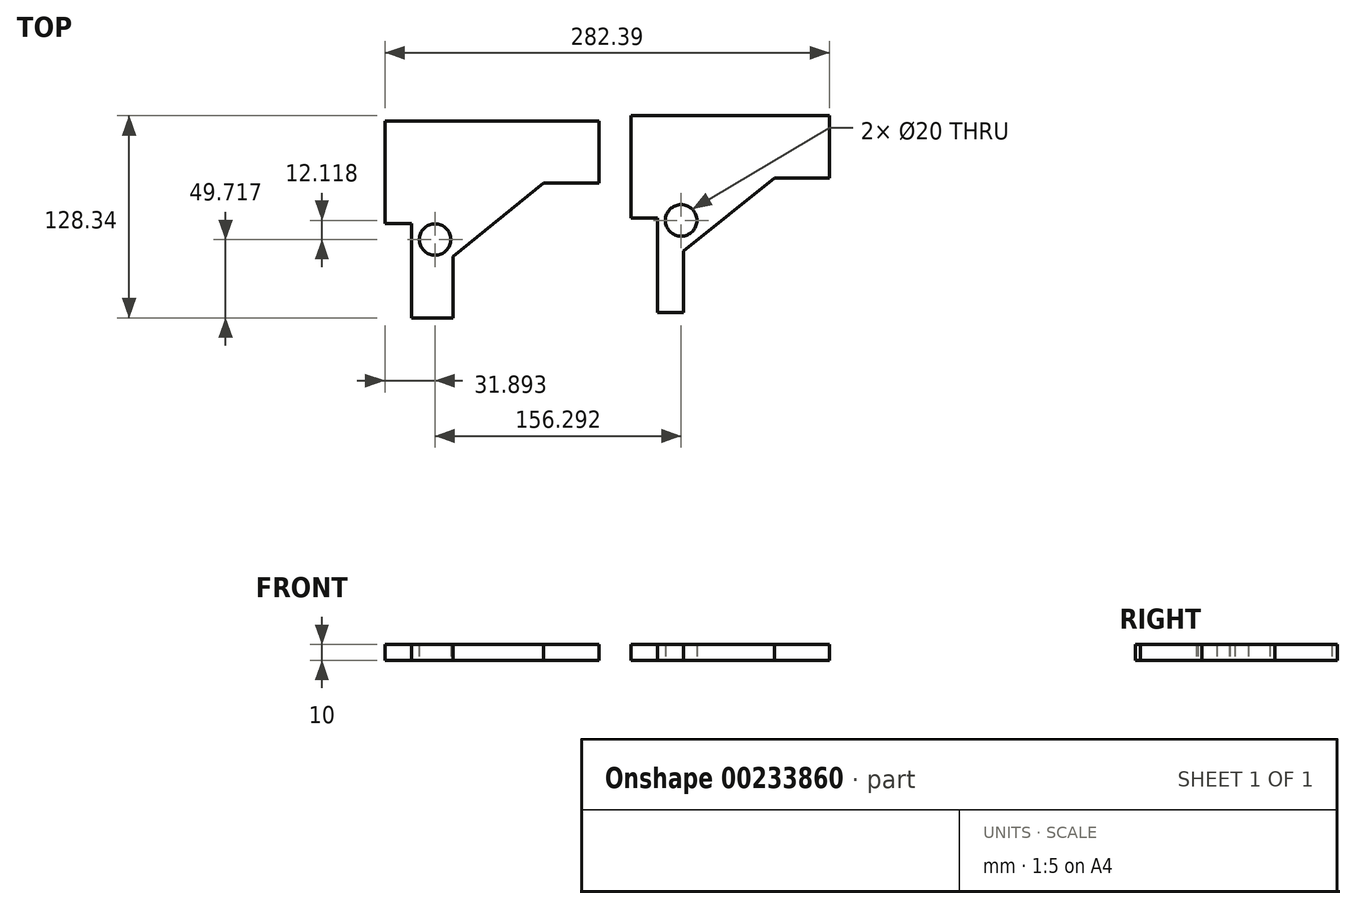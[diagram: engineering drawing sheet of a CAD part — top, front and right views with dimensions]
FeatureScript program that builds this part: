
annotation { "Feature Type Name" : "Feature", "Feature Type Description" : "" }
export const myFeature = defineFeature(function(context is Context, id is Id, definition is map)
    precondition{}
    {
        {
            var Q0;
            Q0=qCreatedBy(makeId("Top.planeOp"),FACE);
            var sketch = newSketch(context, id + "F0", { "sketchPlane" : qUnion([Q0])});
            skLineSegment(sketch, "E0", {"start": v(-69.01, 58.69) * mm, "end": v(-69.01, -6.31) * mm});
            skLineSegment(sketch, "E1", {"start": v(-69.01, -6.31) * mm, "end": v(-52.14, -6.31) * mm});
            skLineSegment(sketch, "E2", {"start": v(-52.14, -6.31) * mm, "end": v(-52.14, -66.31) * mm});
            skLineSegment(sketch, "E3", {"start": v(-52.14, -66.31) * mm, "end": v(-25.64, -66.31) * mm});
            skLineSegment(sketch, "E4", {"start": v(-25.64, -66.31) * mm, "end": v(-25.64, -27.31) * mm});
            skLineSegment(sketch, "E5", {"start": v(-25.64, -27.31) * mm, "end": v(31.92, 19.19) * mm});
            skLineSegment(sketch, "E6", {"start": v(31.92, 19.19) * mm, "end": v(66.92, 19.19) * mm});
            skLineSegment(sketch, "E7", {"start": v(66.92, 19.19) * mm, "end": v(66.92, 58.69) * mm});
            skLineSegment(sketch, "E8", {"start": v(66.92, 58.69) * mm, "end": v(-69.01, 58.69) * mm});
            skCircle(sketch, "E9", {"center": v(-37.12, -16.6) * mm, "radius": 10 * mm});
            skSolve(sketch);
        }
        {
            var Q0;
            Q0=qCreatedBy(makeId("Top.planeOp"),FACE);
            var sketch = newSketch(context, id + "F1", { "sketchPlane" : qUnion([Q0])});
            skLineSegment(sketch, "E10", {"start": v(87.38, 62.03) * mm, "end": v(87.38, -2.97) * mm});
            skLineSegment(sketch, "E11", {"start": v(87.38, -2.97) * mm, "end": v(104.25, -2.97) * mm});
            skLineSegment(sketch, "E12", {"start": v(104.25, -2.97) * mm, "end": v(104.25, -62.97) * mm});
            skLineSegment(sketch, "E13", {"start": v(104.25, -62.97) * mm, "end": v(120.82, -62.97) * mm});
            skLineSegment(sketch, "E14", {"start": v(120.82, -62.97) * mm, "end": v(120.82, -23.97) * mm});
            skLineSegment(sketch, "E15", {"start": v(120.82, -23.97) * mm, "end": v(178.38, 22.53) * mm});
            skLineSegment(sketch, "E16", {"start": v(178.38, 22.53) * mm, "end": v(213.38, 22.53) * mm});
            skLineSegment(sketch, "E17", {"start": v(213.38, 22.53) * mm, "end": v(213.38, 62.03) * mm});
            skLineSegment(sketch, "E18", {"start": v(213.38, 62.03) * mm, "end": v(87.38, 62.03) * mm});
            skCircle(sketch, "E19", {"center": v(119.18, -4.47) * mm, "radius": 10 * mm});
            skSolve(sketch);
        }
        {
            var Q0;
            Q0 = qSketchRegion(id + "F0", true);
            extrude(context, id + "F2", {"entities" : qUnion([Q0]), "depth" : 10 * mm});
        }
        {
            var Q0;
            Q0 = qSketchRegion(id + "F1", true);
            extrude(context, id + "F3", {"entities" : qUnion([Q0]), "depth" : 10 * mm});
        }
    });
